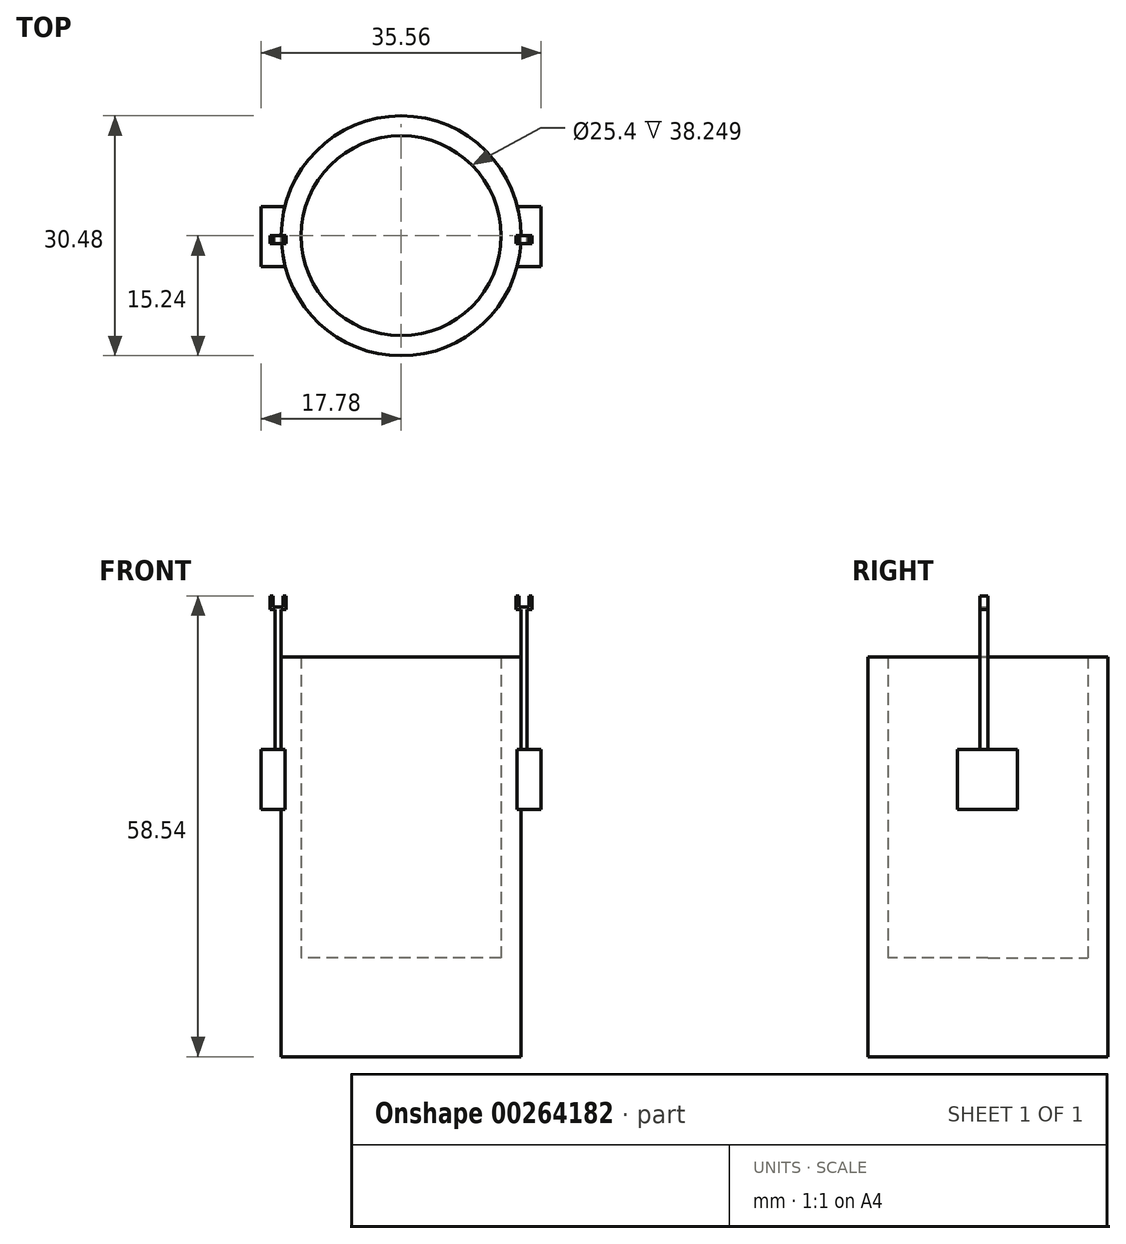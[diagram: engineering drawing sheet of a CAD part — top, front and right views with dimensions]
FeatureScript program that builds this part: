
annotation { "Feature Type Name" : "Feature", "Feature Type Description" : "" }
export const myFeature = defineFeature(function(context is Context, id is Id, definition is map)
    precondition{}
    {
        {
            var Q0;
            Q0=qCreatedBy(makeId("Front.planeOp"),FACE);
            var sketch = newSketch(context, id + "F0", { "sketchPlane" : qUnion([Q0])});
            skLineSegment(sketch, "E0.bottom", {"start": v(-15.24, 38.25) * mm, "end": v(0, 38.25) * mm});
            skLineSegment(sketch, "E0.top", {"start": v(-15.24, -12.55) * mm, "end": v(0, -12.55) * mm});
            skLineSegment(sketch, "E0.left", {"start": v(-15.24, 38.25) * mm, "end": v(-15.24, -12.55) * mm});
            skLineSegment(sketch, "E0.right", {"start": v(0, 38.25) * mm, "end": v(0, -12.55) * mm});
            skSolve(sketch);
        }
        {
            var Q0;
            Q0=makeQuery(id+"F0.imprint","IMPRINT",FACE,{"disambiguationData":[TD([[makeQuery(id+"F0.imprint","IMPRINT",EDGE,{"derivedFrom":sQuery(id+"F0.wireOp",EDGE,"E0.bottom")}),-1.0]])]});
            var Q1;
            Q1=makeQuery(id+"F0.imprint","IMPRINT",FACE,{"disambiguationData":[TD([[makeQuery(id+"F0.imprint","IMPRINT",EDGE,{"derivedFrom":sQuery(id+"F0.wireOp",EDGE,"X9vhU261-cKeK-OZk4-XiLM-RwvlpDQt44RQ.bottom")}),-1.0]])]});
            var Q2;
            Q2=sQuery(id+"F0.wireOp",EDGE,"E0.right");
            revolve(context, id + "F1", {"entities" : qUnion([Q0, Q1]), "axis" : qUnion([Q2]), "revolveType" : RevolveType.FULL});
        }
        {
            var Q0;
            Q0=qCreatedBy(makeId("Right.planeOp"),FACE);
            var sketch = newSketch(context, id + "F2", { "sketchPlane" : qUnion([Q0])});
            skLineSegment(sketch, "E1.bottom", {"start": v(-3.9, 26.47) * mm, "end": v(3.72, 26.47) * mm});
            skLineSegment(sketch, "E1.top", {"start": v(-3.9, 18.85) * mm, "end": v(3.72, 18.85) * mm});
            skLineSegment(sketch, "E1.left", {"start": v(-3.9, 26.47) * mm, "end": v(-3.9, 18.85) * mm});
            skLineSegment(sketch, "E1.right", {"start": v(3.72, 26.47) * mm, "end": v(3.72, 18.85) * mm});
            skSolve(sketch);
        }
        {
            var Q0;
            Q0 = qSketchRegion(id + "F2", true);
            extrude(context, id + "F3", {"entities" : qUnion([Q0]), "operationType" : NewBodyOperationType.ADD, "depth" : 17.78 * mm});
        }
        {
            var Q0;
            Q0=makeQuery(id+"F1.opRevolve","SWEPT_BODY",BODY,{"disambiguationData":[OSD([sQuery(id+"F0.wireOp",EDGE,"E0.bottom"),sQuery(id+"F0.wireOp",EDGE,"E0.top"),sQuery(id+"F0.wireOp",EDGE,"E0.left"),sQuery(id+"F0.wireOp",EDGE,"E0.right")])]});
            var Q1;
            Q1=qCreatedBy(makeId("Right.planeOp"),FACE);
            mirror(context, id + "F4", {"operationType" : NewBodyOperationType.ADD, "entities" : qUnion([Q0]), "mirrorPlane" : qUnion([Q1])});
        }
        {
            var Q0;
            Q0=qCreatedBy(makeId("Front.planeOp"),FACE);
            var sketch = newSketch(context, id + "F5", { "sketchPlane" : qUnion([Q0])});
            skLineSegment(sketch, "E2.bottom", {"start": v(16, 26.47) * mm, "end": v(15.24, 26.47) * mm});
            skLineSegment(sketch, "E2.top", {"start": v(16, 44.25) * mm, "end": v(15.24, 44.25) * mm});
            skLineSegment(sketch, "E2.left", {"start": v(16, 26.47) * mm, "end": v(16, 44.25) * mm});
            skLineSegment(sketch, "E2.right", {"start": v(15.24, 26.47) * mm, "end": v(15.24, 44.25) * mm});
            skLineSegment(sketch, "E3", {"start": v(15.24, 44.25) * mm, "end": v(14.6, 44.25) * mm});
            skLineSegment(sketch, "E4", {"start": v(14.6, 44.25) * mm, "end": v(14.6, 45.99) * mm});
            skLineSegment(sketch, "E5", {"start": v(16, 44.25) * mm, "end": v(16.64, 44.25) * mm});
            skLineSegment(sketch, "E6", {"start": v(16.64, 44.25) * mm, "end": v(16.64, 45.99) * mm});
            skLineSegment(sketch, "E7", {"start": v(16.64, 45.99) * mm, "end": v(16.25, 45.99) * mm});
            skLineSegment(sketch, "E8", {"start": v(16.25, 45.99) * mm, "end": v(16.25, 44.58) * mm});
            skLineSegment(sketch, "E9", {"start": v(16.25, 44.58) * mm, "end": v(15, 44.58) * mm});
            skLineSegment(sketch, "E10", {"start": v(15, 44.58) * mm, "end": v(15, 45.99) * mm});
            skLineSegment(sketch, "E11", {"start": v(15, 45.99) * mm, "end": v(14.6, 45.99) * mm});
            skSolve(sketch);
        }
        {
            var Q0;
            Q0=makeQuery(id+"F5.imprint","IMPRINT",FACE,{"disambiguationData":[TD([[makeQuery(id+"F5.imprint","IMPRINT",EDGE,{"derivedFrom":sQuery(id+"F5.wireOp",EDGE,"E2.top")}),-1.0]])]});
            var Q1;
            Q1=makeQuery(id+"F5.imprint","IMPRINT",FACE,{"disambiguationData":[TD([[makeQuery(id+"F5.imprint","IMPRINT",EDGE,{"derivedFrom":sQuery(id+"F5.wireOp",EDGE,"E2.bottom")}),-1.0]])]});
            extrude(context, id + "F6", {"entities" : qUnion([Q0, Q1]), "operationType" : NewBodyOperationType.ADD, "depth" : 1.02 * mm});
        }
        {
            var Q0;
            Q0=makeQuery(id+"F1.opRevolve","SWEPT_BODY",BODY,{"disambiguationData":[OSD([sQuery(id+"F0.wireOp",EDGE,"E0.bottom"),sQuery(id+"F0.wireOp",EDGE,"E0.top"),sQuery(id+"F0.wireOp",EDGE,"E0.left"),sQuery(id+"F0.wireOp",EDGE,"E0.right")])]});
            var Q1;
            Q1=qCreatedBy(makeId("Right.planeOp"),FACE);
            mirror(context, id + "F7", {"operationType" : NewBodyOperationType.ADD, "entities" : qUnion([Q0]), "mirrorPlane" : qUnion([Q1])});
        }
        {
            var Q0;
            Q0=qCreatedBy(makeId("Top.planeOp"),FACE);
            var sketch = newSketch(context, id + "F8", { "sketchPlane" : qUnion([Q0])});
            skCircle(sketch, "E12", {"center": v(0, 0) * mm, "radius": 12.7 * mm});
            skSolve(sketch);
        }
        {
            var Q0;
            Q0 = qSketchRegion(id + "F8", true);
            extrude(context, id + "F9", {"entities" : qUnion([Q0]), "operationType" : NewBodyOperationType.REMOVE, "depth" : 51.56 * mm});
        }
    });
